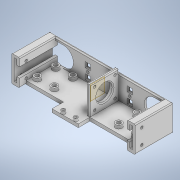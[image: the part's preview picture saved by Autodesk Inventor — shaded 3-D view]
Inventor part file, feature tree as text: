
AUTODESK INVENTOR PART (.ipt)
format: ipt  version: 2022 (Build 260153000, 153)  size: 494,080 bytes
history: native  units: in
note: dims shown in document units (in); Inventor stores cm internally (conversion verified against a paired STEP export)
features: sketch x20, extrude x17, mirror x3, fillet x1, plane x1
ambient origin geometry x8: Origin, YZ Plane, XZ Plane, XY Plane, X Axis, Y Axis, Z Axis, Center Point
bodies: Solid1 (feature_tree)
feature tree (42):
  extrude  "Extrusion1"  Depth=1.8898in
  extrude  "Extrusion2"  Depth=0.1575in
  extrude  "Extrusion3"  Depth=0.1575in
  extrude  "Extrusion4"  Depth=0.1575in
  extrude  "Extrusion5"  Depth=0.1575in
  extrude  "Extrusion6"  Depth=0.315in TaperAngle=0.0deg
  extrude  "Extrusion7"  Depth=0.6102in
  sketch  "Sketch8"  dims[d19=0.315in d20=0.0in d21=0.1575in]
  extrude  "Extrusion8"  Depth=0.1575in
  extrude  "Extrusion9"  Depth=0.3937in TaperAngle=0.0deg
  extrude  "Extrusion10"  Depth=0.2362in
  sketch  "Sketch12"  dims[d29=0.3937in d30=0.0in d31=0.1969in]
  sketch  "Sketch13"  dims[d32=2.9528in d33=1.6654in d34=0.0in]
  extrude  "Extrusion14"  Depth=0.2362in
  mirror  "Mirror2"
  extrude  "Extrusion15"  Depth=0.1969in
  extrude  "Extrusion16"  Depth=1.6654in TaperAngle=0.0deg
  extrude  "Extrusion17"  Depth=0.1575in
  extrude  "Extrusion18"  Depth=0.1575in
  mirror  "Mirror3"
  extrude  "Extrusion19"  Depth=1.6654in TaperAngle=0.0deg
  mirror  "Mirror4"
  fillet  "Fillet1"  Radius=0.3937in
  plane  "Work Plane1"
  extrude  "Extrusion21"  Depth=0.3937in
  sketch  "Sketch1"  dims[d0=7.4016in d1=1.8898in]
  sketch  "Sketch2"  dims[d2=0.1969in d3=0.0in d4=0.1575in]
  sketch  "Sketch3"  dims[d5=0.1575in d6=0.1575in]
  sketch  "Sketch4"  dims[d7=1.378in d8=0.0in d9=0.1575in]
  sketch  "Sketch5"  dims[d10=0.315in d11=0.0in d12=0.1575in]
  sketch  "Sketch6"  dims[d13=0.315in d14=0.0in d15=0.315in d16=0.0in]
  sketch  "Sketch7"  dims[d17=0.4921in d18=0.6102in]
  sketch  "Sketch9"  dims[d22=0.1575in d23=0.3937in d24=0.0in]
  sketch  "Sketch10"  dims[d25=0.2362in d26=0.2362in]
  sketch  "Sketch11"  dims[d27=0.2362in d28=0.2362in]
  sketch  "Sketch17"  dims[d35=0.1575in d36=0.1575in]
  sketch  "Sketch18"  dims[d37=0.1575in d38=0.1575in]
  sketch  "Sketch19"  dims[d39=0.9843in d40=1.6654in d41=0.0in d54=0.3937in]
  sketch  "Sketch20"  dims[d55=0.3937in d56=0.3937in]
  sketch  "Sketch21"  dims[d57=0.3937in]
  sketch  "Sketch22"  dims[d58=0.1969in d59=0.0in]
  sketch  "Sketch24"  dims[d60=1.5748in d61=0.1969in d62=0.689in d63=0.0in d64=0.1575in d65=0.1575in d66=0.689in d67=0.0in d68=0.2362in d69=0.2362in d70=0.1575in d71=0.0in d72=0.1575in d73=0.1575in d74=0.3937in d75=0.3937in d76=0.7874in d77=0.0in d78=0.315in d79=0.315in d80=0.315in d81=0.315in d82=0.1575in d83=0.7874in d84=0.0in d85=0.0591in d92=0.2362in d93=0.2362in d94=0.2362in d95=0.2362in d96=0.1181in d97=0.0in d98=1.4429in d99=0.2224in d100=0.2224in d101=1.4429in d102=0.8327in d103=0.1969in d104=0.2224in d105=0.2224in d106=0.8327in d107=1.4429in d108=1.4429in]
